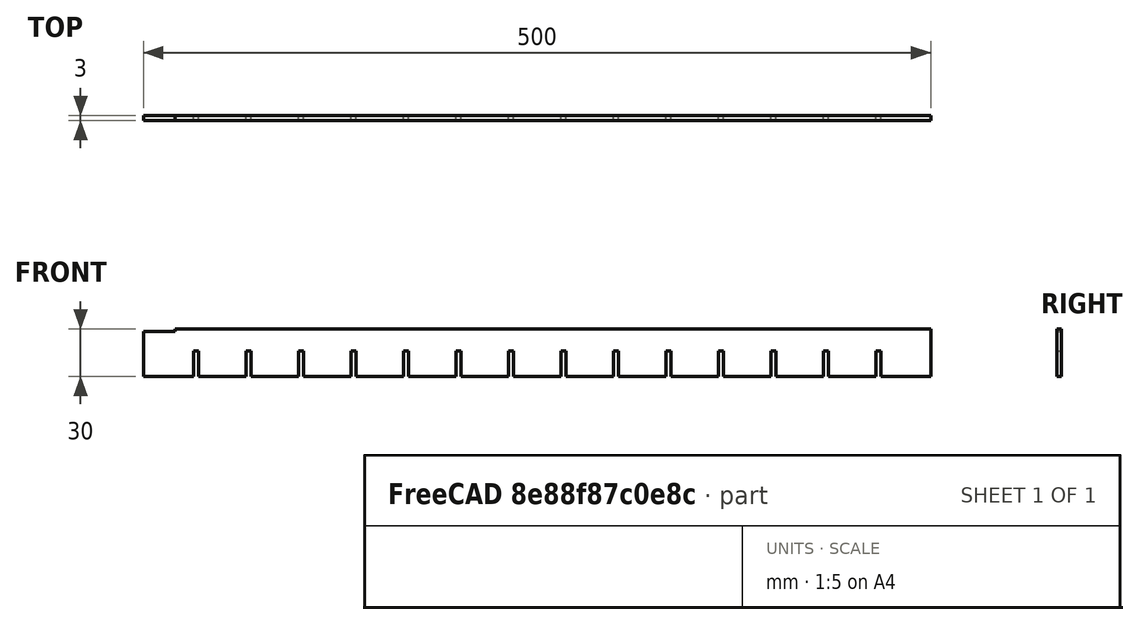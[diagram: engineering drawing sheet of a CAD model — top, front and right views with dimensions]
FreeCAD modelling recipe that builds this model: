
FCSTD DOCUMENT  (FreeCAD 0.16R6527 (Git))
Label: strip_500
License: CC-BY 3.0
LicenseURL: http://creativecommons.org/licenses/by/3.0/
objects: Part::Box×3, Part::Cut×2, Part::FeaturePython×1
note: 6 computed .brp shape members not serialized (recipe doc carries the construction recipe); baked Part::Feature solids carry a one-line shape summary decoded from their .brp

FEATURE [Part::Box] Box  label="Strip"
  Height = 30
  Length = 500
  Width = 3
  expr: Length = bottom#Length - 2 * bottom#Height
FEATURE [Part::Box] Box001  label="Hole"
  Height = 16
  Length = 3
  Placement = pos=(31.8333,0,0) rot=(0,0,1;0rad)
  Width = 3
  expr: Placement.Base.x = 100 / 3 - Strip.Width / 2mm
  expr: Height = Strip.Height / 2 + 1mm
  expr: Length = Strip.Width
  expr: Width = Strip.Width
FEATURE [Part::FeaturePython] Array  # Draft array (typed FeaturePython)
  Angle = 360
  ArrayType = 0
  Axis = (1,0,0)
  Base = -> Box001
  Center = (0,0,0)
  IntervalX = (33.3333,0,0)
  IntervalY = (0,1,0)
  IntervalZ = (0,0,1)
  NumberPolar = 1
  NumberX = 14
  NumberY = 0
  NumberZ = 0
  expr: IntervalX.x = 100 / 3
FEATURE [Part::Cut] Cut
  Base = -> Box
  Tool = -> Array
FEATURE [Part::Box] Box002  label="CablePassing"
  Height = 1.5
  Length = 20
  Placement = pos=(0,0,28.5) rot=(0,0,1;0rad)
  Width = 10
  expr: Placement.Base.z = Strip.Height - CablePassing.Height
FEATURE [Part::Cut] Cut001  label="PiercedStrip"
  Base = -> Cut
  Tool = -> Box002
